# Revit family: MixerSet_Wall_Nero_Celia_Basin_Bath_BackPlate
name_source: partatom
category: Plumbing Fixtures
units: mm (PartAtom-declared; Revit-internal decimal feet)

## family parameters
Always vertical = Yes
Cut with Voids When Loaded = Yes
Maintain Annotation Orientation = No
OmniClass Number = 23.31.11.19
OmniClass Title = Faucet Mixing Valves
Part Type = Normal
Room Calculation Point = No
Round Connector Dimension = Use Diameter
Shared = No
Work Plane-Based = No

## types (3) — shared parameters
Assembly Code = D2010
CW Connection = Yes
Default Elevation = 1050 mm
HW Connection = Yes
IfcExportAs = IfcValveType
IfcExportType = FAUCET
Manufacturer = Nero
ManufacturerOverallDepth = 204.5 mm
ManufacturerOverallHeight = 120 mm
ManufacturerOverallWidth = 180 mm
ManufacturerURLProductSpecific = https://nerotapware.com.au
ModifiedIssue = 20251105 $
URL = D2010
Uniclass2015Code = Pr_40_20_87
Uniclass2015Title = Taps and water supply outlet fittings
Uniclass2015Version = Products v1.35
Vent Connection = No
Waste Connection = No
zero-valued in all types: CWFU, HWFU, WFU

## per-type parameters (varying)
| type | Description | ManufacturerSpecCode | Material | Model | Type Comments |
| Matte Black (NR301510bMB) | Celia Wall Basin/Bath Mixer Separate Back Plate Matte Black | NR301510bMB | Metal_MatteBlack_Nero | NR301510bMB | Mixer Set - Wall - Basin - Bath - Back Plate - Matte Black |
| Brushed Nickel (NR301510bBN) | Celia Wall Basin/Bath Mixer Separate Back Plate Brushed Nickel | NR301510bBN | Metal_Nickel_Nero_Brushed | NR301510bBN | Mixer Set - Wall - Basin - Bath - Back Plate - Brushed Nickel |
| Chrome (NR301510bCH) | Celia Wall Basin/Bath Mixer Separate Back Plate Chrome | NR301510bCH | Metal_Chrome_Nero | NR301510bCH | Mixer Set - Wall - Basin - Bath - Back Plate - Chrome |

## geometry (parser evidence)
native form markers: Sweep x2
no freeform markers — native parametric forms only
